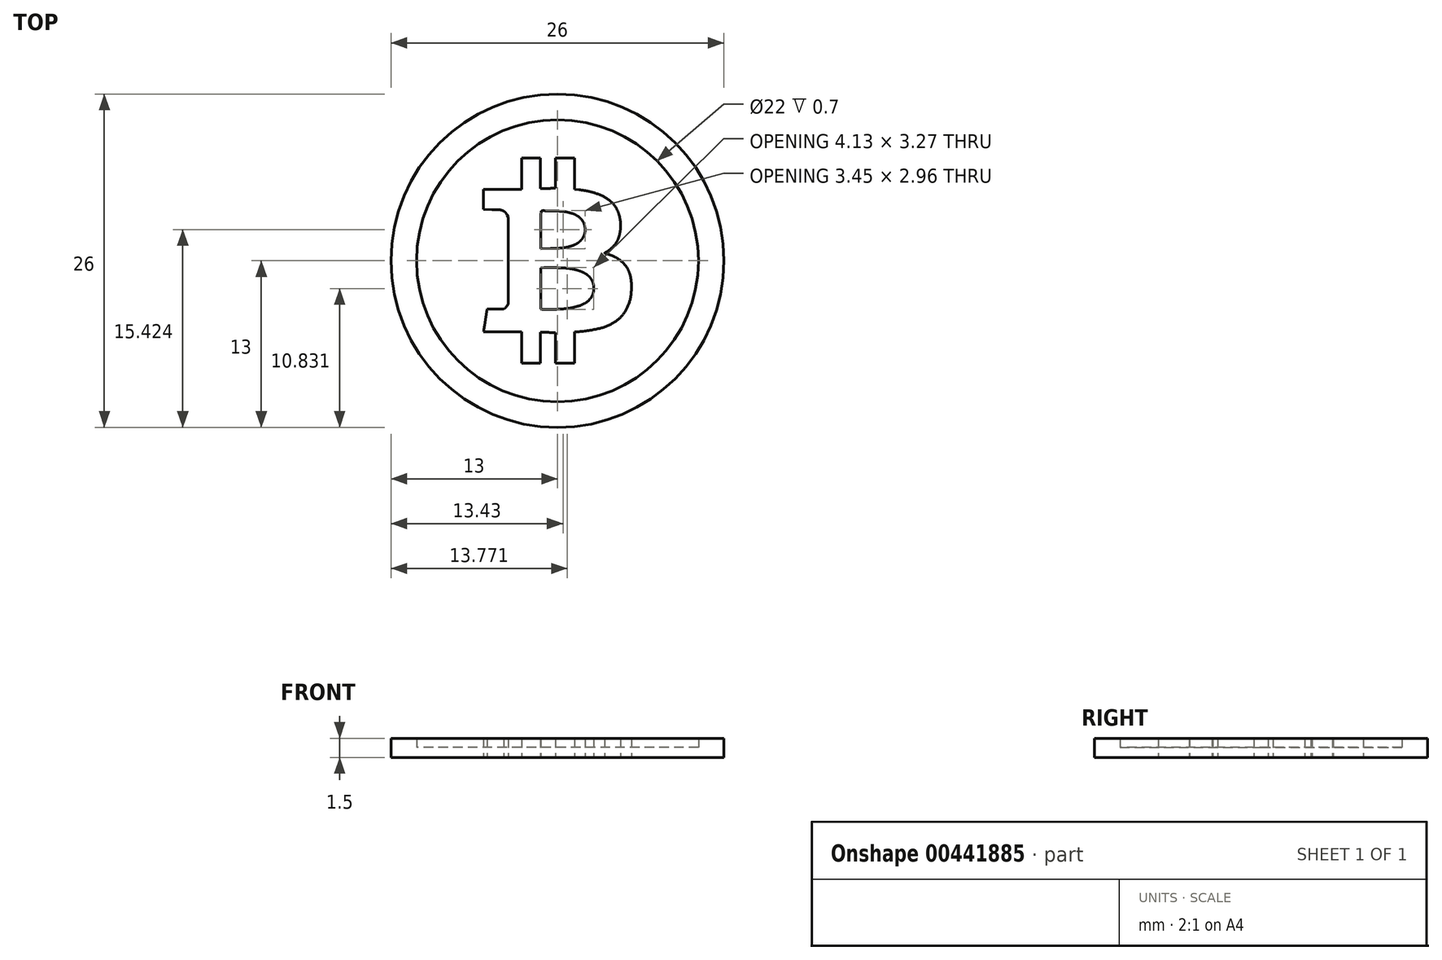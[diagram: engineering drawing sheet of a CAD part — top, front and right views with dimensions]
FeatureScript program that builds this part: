
annotation { "Feature Type Name" : "Feature", "Feature Type Description" : "" }
export const myFeature = defineFeature(function(context is Context, id is Id, definition is map)
    precondition{}
    {
        {
            var Q0;
            Q0=qCreatedBy(makeId("Top.planeOp"),FACE);
            var sketch = newSketch(context, id + "F0", { "sketchPlane" : qUnion([Q0])});
            skCircle(sketch, "E0", {"center": v(0, 0) * mm, "radius": 13 * mm});
            skCircle(sketch, "E1", {"center": v(0, 0) * mm, "radius": 11 * mm});
            skSolve(sketch);
        }
        {
            var Q0;
            Q0=makeQuery(id+"F0.imprint","IMPRINT",FACE,{"disambiguationData":[TD([[makeQuery(id+"F0.imprint","IMPRINT",EDGE,{"derivedFrom":sQuery(id+"F0.wireOp",EDGE,"E1")}),1.0]])]});
            extrude(context, id + "F1", {"entities" : qUnion([Q0]), "depth" : 0.8 * mm});
        }
        {
            var Q0;
            Q0 = qSketchRegion(id + "F0", true);
            extrude(context, id + "F2", {"entities" : qUnion([Q0]), "operationType" : NewBodyOperationType.ADD, "depth" : 1.5 * mm});
        }
        {
            var Q0;
            Q0=qCreatedBy(makeId("Top.planeOp"),FACE);
            var sketch = newSketch(context, id + "F3", { "sketchPlane" : qUnion([Q0])});
            skLineSegment(sketch, "E2", {"start": v(-111.79, 271.5) * mm, "end": v(-111.79, 223) * mm});
            skLineSegment(sketch, "E3", {"start": v(-111.79, 223) * mm, "end": v(-171.29, 223) * mm});
            skLineSegment(sketch, "E4", {"start": v(-171.29, 223) * mm, "end": v(-230.79, 223) * mm});
            skLineSegment(sketch, "E5", {"start": v(-230.79, 223) * mm, "end": v(-230.79, 191.59) * mm});
            skLineSegment(sketch, "E6", {"start": v(-230.79, 191.59) * mm, "end": v(-230.79, 160.17) * mm});
            skLineSegment(sketch, "E7", {"start": v(-230.79, 160.17) * mm, "end": v(-204.54, 159.8) * mm});
            skArc(sketch, "E8", {"start": v(-204.54, 159.8) * mm, "mid": v(-196.82, 159.67) * mm, "end": v(-189.1, 159.51) * mm});
            skArc(sketch, "E9", {"start": v(-189.1, 159.51) * mm, "mid": v(-185.4, 159.38) * mm, "end": v(-181.7, 159.14) * mm});
            skArc(sketch, "E10", {"start": v(-181.7, 159.14) * mm, "mid": v(-179.35, 158.9) * mm, "end": v(-177.03, 158.5) * mm});
            skArc(sketch, "E11", {"start": v(-177.03, 158.5) * mm, "mid": v(-175.06, 158.02) * mm, "end": v(-173.16, 157.35) * mm});
            skArc(sketch, "E12", {"start": v(-173.16, 157.35) * mm, "mid": v(-170.43, 156.14) * mm, "end": v(-167.78, 154.75) * mm});
            skArc(sketch, "E13", {"start": v(-167.78, 154.75) * mm, "mid": v(-165.66, 153.39) * mm, "end": v(-163.7, 151.8) * mm});
            skArc(sketch, "E14", {"start": v(-163.7, 151.8) * mm, "mid": v(-161.97, 150.03) * mm, "end": v(-160.44, 148.07) * mm});
            skArc(sketch, "E15", {"start": v(-160.44, 148.07) * mm, "mid": v(-158.9, 145.67) * mm, "end": v(-157.55, 143.16) * mm});
            skLineSegment(sketch, "E16", {"start": v(-157.55, 143.16) * mm, "end": v(-154.29, 136.54) * mm});
            skLineSegment(sketch, "E17", {"start": v(-154.29, 136.54) * mm, "end": v(-154.29, 1.02) * mm});
            skLineSegment(sketch, "E18", {"start": v(-154.29, 1.02) * mm, "end": v(-154.29, -134.5) * mm});
            skLineSegment(sketch, "E19", {"start": v(-154.29, -134.5) * mm, "end": v(-156.79, -139.5) * mm});
            skArc(sketch, "E20", {"start": v(-156.79, -139.5) * mm, "mid": v(-157.42, -140.67) * mm, "end": v(-158.13, -141.8) * mm});
            skArc(sketch, "E21", {"start": v(-158.13, -141.8) * mm, "mid": v(-158.92, -142.9) * mm, "end": v(-159.77, -143.96) * mm});
            skArc(sketch, "E22", {"start": v(-159.77, -143.96) * mm, "mid": v(-160.67, -144.96) * mm, "end": v(-161.63, -145.9) * mm});
            skArc(sketch, "E23", {"start": v(-161.63, -145.9) * mm, "mid": v(-162.6, -146.73) * mm, "end": v(-163.62, -147.5) * mm});
            skLineSegment(sketch, "E24", {"start": v(-163.62, -147.5) * mm, "end": v(-167.96, -150.5) * mm});
            skLineSegment(sketch, "E25", {"start": v(-167.96, -150.5) * mm, "end": v(-193.68, -150.81) * mm});
            skLineSegment(sketch, "E26", {"start": v(-193.68, -150.81) * mm, "end": v(-219.4, -151.12) * mm});
            skLineSegment(sketch, "E27", {"start": v(-219.4, -151.12) * mm, "end": v(-224.7, -183.81) * mm});
            skArc(sketch, "E28", {"start": v(-224.7, -183.81) * mm, "mid": v(-225.73, -190.17) * mm, "end": v(-226.76, -196.54) * mm});
            skArc(sketch, "E29", {"start": v(-226.76, -196.54) * mm, "mid": v(-227.67, -202.12) * mm, "end": v(-228.59, -207.7) * mm});
            skArc(sketch, "E30", {"start": v(-228.59, -207.7) * mm, "mid": v(-229.37, -212.47) * mm, "end": v(-230.15, -217.24) * mm});
            skArc(sketch, "E31", {"start": v(-230.15, -217.24) * mm, "mid": v(-230.33, -218.24) * mm, "end": v(-230.51, -219.25) * mm});
            skLineSegment(sketch, "E32", {"start": v(-230.51, -219.25) * mm, "end": v(-231.04, -222) * mm});
            skLineSegment(sketch, "E33", {"start": v(-231.04, -222) * mm, "end": v(-171.41, -222) * mm});
            skLineSegment(sketch, "E34", {"start": v(-171.41, -222) * mm, "end": v(-111.79, -222) * mm});
            skLineSegment(sketch, "E35", {"start": v(-111.79, -222) * mm, "end": v(-111.79, -271) * mm});
            skLineSegment(sketch, "E36", {"start": v(-111.79, -271) * mm, "end": v(-111.79, -320) * mm});
            skLineSegment(sketch, "E37", {"start": v(-111.79, -320) * mm, "end": v(-82.29, -320) * mm});
            skLineSegment(sketch, "E38", {"start": v(-82.29, -320) * mm, "end": v(-52.79, -320) * mm});
            skLineSegment(sketch, "E39", {"start": v(-52.79, -320) * mm, "end": v(-52.79, -271.34) * mm});
            skLineSegment(sketch, "E40", {"start": v(-52.79, -271.34) * mm, "end": v(-52.79, -222.69) * mm});
            skLineSegment(sketch, "E41", {"start": v(-52.79, -222.69) * mm, "end": v(-35.54, -223.34) * mm});
            skArc(sketch, "E42", {"start": v(-35.54, -223.34) * mm, "mid": v(-32, -223.47) * mm, "end": v(-28.48, -223.6) * mm});
            skArc(sketch, "E43", {"start": v(-28.48, -223.6) * mm, "mid": v(-25, -223.7) * mm, "end": v(-21.52, -223.8) * mm});
            skArc(sketch, "E44", {"start": v(-21.52, -223.8) * mm, "mid": v(-18.52, -223.88) * mm, "end": v(-15.51, -223.96) * mm});
            skArc(sketch, "E45", {"start": v(-15.51, -223.96) * mm, "mid": v(-13.78, -223.99) * mm, "end": v(-12.04, -224) * mm});
            skLineSegment(sketch, "E46", {"start": v(-12.04, -224) * mm, "end": v(-5.79, -224) * mm});
            skLineSegment(sketch, "E47", {"start": v(-5.79, -224) * mm, "end": v(-5.79, -272) * mm});
            skLineSegment(sketch, "E48", {"start": v(-5.79, -272) * mm, "end": v(-5.79, -320) * mm});
            skLineSegment(sketch, "E49", {"start": v(-5.79, -320) * mm, "end": v(23.71, -320) * mm});
            skLineSegment(sketch, "E50", {"start": v(23.71, -320) * mm, "end": v(53.21, -320) * mm});
            skLineSegment(sketch, "E51", {"start": v(53.21, -320) * mm, "end": v(53.21, -271.14) * mm});
            skLineSegment(sketch, "E52", {"start": v(53.21, -271.14) * mm, "end": v(53.21, -222.27) * mm});
            skLineSegment(sketch, "E53", {"start": v(53.21, -222.27) * mm, "end": v(62.96, -221.59) * mm});
            skArc(sketch, "E54", {"start": v(62.96, -221.59) * mm, "mid": v(97.45, -217.74) * mm, "end": v(131.53, -211.13) * mm});
            skArc(sketch, "E55", {"start": v(131.53, -211.13) * mm, "mid": v(156.79, -202.75) * mm, "end": v(180.2, -190.07) * mm});
            skArc(sketch, "E56", {"start": v(180.2, -190.07) * mm, "mid": v(197.76, -175.43) * mm, "end": v(211.68, -157.3) * mm});
            skArc(sketch, "E57", {"start": v(211.68, -157.3) * mm, "mid": v(222.29, -135.43) * mm, "end": v(228.69, -112) * mm});
            skArc(sketch, "E58", {"start": v(228.69, -112) * mm, "mid": v(229.06, -109.66) * mm, "end": v(229.37, -107.3) * mm});
            skArc(sketch, "E59", {"start": v(229.37, -107.3) * mm, "mid": v(229.72, -104.08) * mm, "end": v(230.03, -100.85) * mm});
            skArc(sketch, "E60", {"start": v(230.03, -100.85) * mm, "mid": v(230.33, -97.36) * mm, "end": v(230.58, -93.86) * mm});
            skArc(sketch, "E61", {"start": v(230.58, -93.86) * mm, "mid": v(230.78, -90.62) * mm, "end": v(230.92, -87.38) * mm});
            skArc(sketch, "E62", {"start": v(230.92, -87.38) * mm, "mid": v(230.7, -70.42) * mm, "end": v(228.76, -53.56) * mm});
            skArc(sketch, "E63", {"start": v(228.76, -53.56) * mm, "mid": v(225.24, -39.46) * mm, "end": v(219.52, -26.1) * mm});
            skArc(sketch, "E64", {"start": v(219.52, -26.1) * mm, "mid": v(212.07, -14.5) * mm, "end": v(202.75, -4.37) * mm});
            skArc(sketch, "E65", {"start": v(202.75, -4.37) * mm, "mid": v(191.14, 4.87) * mm, "end": v(178.37, 12.43) * mm});
            skArc(sketch, "E66", {"start": v(178.37, 12.43) * mm, "mid": v(175, 14.03) * mm, "end": v(171.57, 15.48) * mm});
            skArc(sketch, "E67", {"start": v(171.57, 15.48) * mm, "mid": v(166.77, 17.34) * mm, "end": v(161.94, 19.11) * mm});
            skArc(sketch, "E68", {"start": v(161.94, 19.11) * mm, "mid": v(157.15, 20.8) * mm, "end": v(152.34, 22.43) * mm});
            skArc(sketch, "E69", {"start": v(152.34, 22.43) * mm, "mid": v(150.6, 22.86) * mm, "end": v(148.83, 23) * mm});
            skArc(sketch, "E70", {"start": v(148.83, 23) * mm, "mid": v(148.25, 23.1) * mm, "end": v(147.73, 23.4) * mm});
            skArc(sketch, "E71", {"start": v(147.73, 23.4) * mm, "mid": v(147.53, 23.77) * mm, "end": v(147.67, 24.16) * mm});
            skArc(sketch, "E72", {"start": v(147.67, 24.16) * mm, "mid": v(148.47, 24.94) * mm, "end": v(149.37, 25.6) * mm});
            skArc(sketch, "E73", {"start": v(149.37, 25.6) * mm, "mid": v(151.31, 26.79) * mm, "end": v(153.27, 27.94) * mm});
            skArc(sketch, "E74", {"start": v(153.27, 27.94) * mm, "mid": v(157.98, 30.87) * mm, "end": v(162.46, 34.13) * mm});
            skArc(sketch, "E75", {"start": v(162.46, 34.13) * mm, "mid": v(167.05, 37.98) * mm, "end": v(171.42, 42.08) * mm});
            skArc(sketch, "E76", {"start": v(171.42, 42.08) * mm, "mid": v(175.53, 46.42) * mm, "end": v(179.39, 51) * mm});
            skArc(sketch, "E77", {"start": v(179.39, 51) * mm, "mid": v(182.66, 55.45) * mm, "end": v(185.6, 60.14) * mm});
            skArc(sketch, "E78", {"start": v(185.6, 60.14) * mm, "mid": v(188.11, 65) * mm, "end": v(190.18, 70.07) * mm});
            skArc(sketch, "E79", {"start": v(190.18, 70.07) * mm, "mid": v(192.2, 76.3) * mm, "end": v(193.9, 82.64) * mm});
            skArc(sketch, "E80", {"start": v(193.9, 82.64) * mm, "mid": v(195.32, 89.32) * mm, "end": v(196.39, 96.06) * mm});
            skArc(sketch, "E81", {"start": v(196.39, 96.06) * mm, "mid": v(197, 102.33) * mm, "end": v(197.2, 108.63) * mm});
            skArc(sketch, "E82", {"start": v(197.2, 108.63) * mm, "mid": v(195.94, 126.5) * mm, "end": v(192.21, 144.03) * mm});
            skArc(sketch, "E83", {"start": v(192.21, 144.03) * mm, "mid": v(186.31, 159.12) * mm, "end": v(177.7, 172.86) * mm});
            skArc(sketch, "E84", {"start": v(177.7, 172.86) * mm, "mid": v(166.49, 185.05) * mm, "end": v(153.26, 195.03) * mm});
            skArc(sketch, "E85", {"start": v(153.26, 195.03) * mm, "mid": v(136.62, 203.98) * mm, "end": v(119.02, 210.82) * mm});
            skArc(sketch, "E86", {"start": v(119.02, 210.82) * mm, "mid": v(113.11, 212.62) * mm, "end": v(107.16, 214.26) * mm});
            skArc(sketch, "E87", {"start": v(107.16, 214.26) * mm, "mid": v(100.9, 215.8) * mm, "end": v(94.63, 217.2) * mm});
            skArc(sketch, "E88", {"start": v(94.63, 217.2) * mm, "mid": v(88.03, 218.5) * mm, "end": v(81.4, 219.66) * mm});
            skArc(sketch, "E89", {"start": v(81.4, 219.66) * mm, "mid": v(74.44, 220.72) * mm, "end": v(67.46, 221.63) * mm});
            skLineSegment(sketch, "E90", {"start": v(67.46, 221.63) * mm, "end": v(53.21, 223.35) * mm});
            skLineSegment(sketch, "E91", {"start": v(53.21, 223.35) * mm, "end": v(53.21, 271.68) * mm});
            skLineSegment(sketch, "E92", {"start": v(53.21, 271.68) * mm, "end": v(53.21, 320) * mm});
            skLineSegment(sketch, "E93", {"start": v(53.21, 320) * mm, "end": v(23.71, 320) * mm});
            skLineSegment(sketch, "E94", {"start": v(23.71, 320) * mm, "end": v(-5.79, 320) * mm});
            skLineSegment(sketch, "E95", {"start": v(-5.79, 320) * mm, "end": v(-5.79, 273) * mm});
            skLineSegment(sketch, "E96", {"start": v(-5.79, 273) * mm, "end": v(-5.79, 226) * mm});
            skLineSegment(sketch, "E97", {"start": v(-5.79, 226) * mm, "end": v(-15.04, 226) * mm});
            skArc(sketch, "E98", {"start": v(-15.04, 226) * mm, "mid": v(-17.3, 225.98) * mm, "end": v(-19.58, 225.95) * mm});
            skArc(sketch, "E99", {"start": v(-19.58, 225.95) * mm, "mid": v(-22.67, 225.88) * mm, "end": v(-25.76, 225.8) * mm});
            skArc(sketch, "E100", {"start": v(-25.76, 225.8) * mm, "mid": v(-29.08, 225.7) * mm, "end": v(-32.4, 225.6) * mm});
            skArc(sketch, "E101", {"start": v(-32.4, 225.6) * mm, "mid": v(-35.47, 225.47) * mm, "end": v(-38.54, 225.34) * mm});
            skLineSegment(sketch, "E102", {"start": v(-38.54, 225.34) * mm, "end": v(-52.79, 224.69) * mm});
            skLineSegment(sketch, "E103", {"start": v(-52.79, 224.69) * mm, "end": v(-52.79, 272.34) * mm});
            skLineSegment(sketch, "E104", {"start": v(-52.79, 272.34) * mm, "end": v(-52.79, 320) * mm});
            skLineSegment(sketch, "E105", {"start": v(-52.79, 320) * mm, "end": v(-82.29, 320) * mm});
            skLineSegment(sketch, "E106", {"start": v(-82.29, 320) * mm, "end": v(-111.79, 320) * mm});
            skLineSegment(sketch, "E107", {"start": v(-111.79, 320) * mm, "end": v(-111.79, 271.5) * mm});
            skArc(sketch, "E108", {"start": v(21.03, 153.53) * mm, "mid": v(33.98, 150.93) * mm, "end": v(46.66, 147.27) * mm});
            skArc(sketch, "E109", {"start": v(46.66, 147.27) * mm, "mid": v(56.59, 143.11) * mm, "end": v(65.78, 137.51) * mm});
            skArc(sketch, "E110", {"start": v(65.78, 137.51) * mm, "mid": v(72.75, 131.46) * mm, "end": v(78.48, 124.24) * mm});
            skArc(sketch, "E111", {"start": v(78.48, 124.24) * mm, "mid": v(82.64, 116.23) * mm, "end": v(85.13, 107.57) * mm});
            skArc(sketch, "E112", {"start": v(85.13, 107.57) * mm, "mid": v(85.98, 101.07) * mm, "end": v(86.19, 94.52) * mm});
            skArc(sketch, "E113", {"start": v(86.19, 94.52) * mm, "mid": v(85.68, 88.64) * mm, "end": v(84.39, 82.87) * mm});
            skArc(sketch, "E114", {"start": v(84.39, 82.87) * mm, "mid": v(82.35, 77.4) * mm, "end": v(79.58, 72.28) * mm});
            skArc(sketch, "E115", {"start": v(79.58, 72.28) * mm, "mid": v(75.93, 67.12) * mm, "end": v(71.73, 62.4) * mm});
            skArc(sketch, "E116", {"start": v(71.73, 62.4) * mm, "mid": v(68.5, 59.37) * mm, "end": v(65.05, 56.6) * mm});
            skArc(sketch, "E117", {"start": v(65.05, 56.6) * mm, "mid": v(61.34, 54.07) * mm, "end": v(57.46, 51.81) * mm});
            skArc(sketch, "E118", {"start": v(57.46, 51.81) * mm, "mid": v(53.11, 49.68) * mm, "end": v(48.63, 47.85) * mm});
            skArc(sketch, "E119", {"start": v(48.63, 47.85) * mm, "mid": v(43.45, 46.08) * mm, "end": v(38.2, 44.55) * mm});
            skArc(sketch, "E120", {"start": v(38.2, 44.55) * mm, "mid": v(31.88, 42.98) * mm, "end": v(25.52, 41.63) * mm});
            skArc(sketch, "E121", {"start": v(25.52, 41.63) * mm, "mid": v(19.68, 40.62) * mm, "end": v(13.8, 39.87) * mm});
            skArc(sketch, "E122", {"start": v(13.8, 39.87) * mm, "mid": v(6.76, 39.25) * mm, "end": v(-0.3, 38.86) * mm});
            skArc(sketch, "E123", {"start": v(-0.3, 38.86) * mm, "mid": v(-10.92, 38.52) * mm, "end": v(-21.54, 38.28) * mm});
            skLineSegment(sketch, "E124", {"start": v(-21.54, 38.28) * mm, "end": v(-51.79, 37.75) * mm});
            skLineSegment(sketch, "E125", {"start": v(-51.79, 37.75) * mm, "end": v(-51.79, 96.3) * mm});
            skArc(sketch, "E126", {"start": v(-51.79, 96.3) * mm, "mid": v(-51.78, 114.38) * mm, "end": v(-51.75, 132.46) * mm});
            skArc(sketch, "E127", {"start": v(-51.75, 132.46) * mm, "mid": v(-51.69, 139.35) * mm, "end": v(-51.53, 146.24) * mm});
            skArc(sketch, "E128", {"start": v(-51.53, 146.24) * mm, "mid": v(-51.38, 150.11) * mm, "end": v(-51.15, 153.98) * mm});
            skArc(sketch, "E129", {"start": v(-51.15, 153.98) * mm, "mid": v(-50.81, 154.85) * mm, "end": v(-50.04, 155.38) * mm});
            skArc(sketch, "E130", {"start": v(-50.04, 155.38) * mm, "mid": v(-47.25, 155.98) * mm, "end": v(-44.4, 156.15) * mm});
            skArc(sketch, "E131", {"start": v(-44.4, 156.15) * mm, "mid": v(-30.57, 155.86) * mm, "end": v(-16.75, 155.52) * mm});
            skArc(sketch, "E132", {"start": v(-16.75, 155.52) * mm, "mid": v(-3.61, 155.14) * mm, "end": v(9.52, 154.67) * mm});
            skArc(sketch, "E133", {"start": v(9.52, 154.67) * mm, "mid": v(15.3, 154.27) * mm, "end": v(21.03, 153.53) * mm});
            skArc(sketch, "E134", {"start": v(30.21, -23.44) * mm, "mid": v(42.62, -25.24) * mm, "end": v(54.91, -27.67) * mm});
            skArc(sketch, "E135", {"start": v(54.91, -27.67) * mm, "mid": v(65.12, -30.43) * mm, "end": v(75.05, -34.04) * mm});
            skArc(sketch, "E136", {"start": v(75.05, -34.04) * mm, "mid": v(83.16, -37.9) * mm, "end": v(90.82, -42.55) * mm});
            skArc(sketch, "E137", {"start": v(90.82, -42.55) * mm, "mid": v(96.96, -47.44) * mm, "end": v(102.29, -53.22) * mm});
            skArc(sketch, "E138", {"start": v(102.29, -53.22) * mm, "mid": v(104.9, -56.81) * mm, "end": v(107.24, -60.6) * mm});
            skArc(sketch, "E139", {"start": v(107.24, -60.6) * mm, "mid": v(109.13, -64.38) * mm, "end": v(110.68, -68.31) * mm});
            skArc(sketch, "E140", {"start": v(110.68, -68.31) * mm, "mid": v(111.88, -72.44) * mm, "end": v(112.7, -76.67) * mm});
            skArc(sketch, "E141", {"start": v(112.7, -76.67) * mm, "mid": v(113.24, -81.32) * mm, "end": v(113.45, -86) * mm});
            skArc(sketch, "E142", {"start": v(113.45, -86) * mm, "mid": v(112.15, -98) * mm, "end": v(108.1, -109.37) * mm});
            skArc(sketch, "E143", {"start": v(108.1, -109.37) * mm, "mid": v(101.52, -119.5) * mm, "end": v(92.78, -127.83) * mm});
            skArc(sketch, "E144", {"start": v(92.78, -127.83) * mm, "mid": v(80.33, -135.58) * mm, "end": v(66.72, -141.05) * mm});
            skArc(sketch, "E145", {"start": v(66.72, -141.05) * mm, "mid": v(48.38, -145.77) * mm, "end": v(29.71, -148.96) * mm});
            skArc(sketch, "E146", {"start": v(29.71, -148.96) * mm, "mid": v(21.14, -149.9) * mm, "end": v(12.54, -150.55) * mm});
            skArc(sketch, "E147", {"start": v(12.54, -150.55) * mm, "mid": v(0.42, -151.17) * mm, "end": v(-11.71, -151.63) * mm});
            skArc(sketch, "E148", {"start": v(-11.71, -151.63) * mm, "mid": v(-23.56, -151.93) * mm, "end": v(-35.4, -152.1) * mm});
            skArc(sketch, "E149", {"start": v(-35.4, -152.1) * mm, "mid": v(-41.29, -151.95) * mm, "end": v(-47.15, -151.36) * mm});
            skLineSegment(sketch, "E150", {"start": v(-47.15, -151.36) * mm, "end": v(-51.79, -150.73) * mm});
            skLineSegment(sketch, "E151", {"start": v(-51.79, -150.73) * mm, "end": v(-51.79, -86.4) * mm});
            skLineSegment(sketch, "E152", {"start": v(-51.79, -86.4) * mm, "end": v(-51.79, -22.07) * mm});
            skLineSegment(sketch, "E153", {"start": v(-51.79, -22.07) * mm, "end": v(-41.54, -21.67) * mm});
            skArc(sketch, "E154", {"start": v(-41.54, -21.67) * mm, "mid": v(-33.33, -21.44) * mm, "end": v(-25.12, -21.4) * mm});
            skArc(sketch, "E155", {"start": v(-25.12, -21.4) * mm, "mid": v(-14.26, -21.5) * mm, "end": v(-3.4, -21.72) * mm});
            skArc(sketch, "E156", {"start": v(-3.4, -21.72) * mm, "mid": v(7.1, -22.02) * mm, "end": v(17.6, -22.42) * mm});
            skArc(sketch, "E157", {"start": v(17.6, -22.42) * mm, "mid": v(23.92, -22.81) * mm, "end": v(30.21, -23.44) * mm});
            skSolve(sketch);
        }
        {
            var Q0;
            Q0 = qSketchRegion(id + "F3", true);
            extrude(context, id + "F4", {"entities" : qUnion([Q0]), "depth" : 60 * mm});
        }
        {
            var Q0;
            Q0=makeQuery(id+"F4.opExtrude","SWEPT_BODY",BODY,{"disambiguationData":[OSD([sQuery(id+"F3.wireOp",EDGE,"E2"),sQuery(id+"F3.wireOp",EDGE,"E3"),sQuery(id+"F3.wireOp",EDGE,"E4"),sQuery(id+"F3.wireOp",EDGE,"E5"),sQuery(id+"F3.wireOp",EDGE,"E6"),sQuery(id+"F3.wireOp",EDGE,"E7"),sQuery(id+"F3.wireOp",EDGE,"E8"),sQuery(id+"F3.wireOp",EDGE,"E9"),sQuery(id+"F3.wireOp",EDGE,"E10"),sQuery(id+"F3.wireOp",EDGE,"E11"),sQuery(id+"F3.wireOp",EDGE,"E12"),sQuery(id+"F3.wireOp",EDGE,"E13"),sQuery(id+"F3.wireOp",EDGE,"E14"),sQuery(id+"F3.wireOp",EDGE,"E15"),sQuery(id+"F3.wireOp",EDGE,"E16"),sQuery(id+"F3.wireOp",EDGE,"E17"),sQuery(id+"F3.wireOp",EDGE,"E18"),sQuery(id+"F3.wireOp",EDGE,"E19"),sQuery(id+"F3.wireOp",EDGE,"E20"),sQuery(id+"F3.wireOp",EDGE,"E21"),sQuery(id+"F3.wireOp",EDGE,"E22"),sQuery(id+"F3.wireOp",EDGE,"E23"),sQuery(id+"F3.wireOp",EDGE,"E24"),sQuery(id+"F3.wireOp",EDGE,"E25"),sQuery(id+"F3.wireOp",EDGE,"E26"),sQuery(id+"F3.wireOp",EDGE,"E27"),sQuery(id+"F3.wireOp",EDGE,"E28"),sQuery(id+"F3.wireOp",EDGE,"E29"),sQuery(id+"F3.wireOp",EDGE,"E30"),sQuery(id+"F3.wireOp",EDGE,"E31"),sQuery(id+"F3.wireOp",EDGE,"E32"),sQuery(id+"F3.wireOp",EDGE,"E33"),sQuery(id+"F3.wireOp",EDGE,"E34"),sQuery(id+"F3.wireOp",EDGE,"E35"),sQuery(id+"F3.wireOp",EDGE,"E36"),sQuery(id+"F3.wireOp",EDGE,"E37"),sQuery(id+"F3.wireOp",EDGE,"E38"),sQuery(id+"F3.wireOp",EDGE,"E39"),sQuery(id+"F3.wireOp",EDGE,"E40"),sQuery(id+"F3.wireOp",EDGE,"E41"),sQuery(id+"F3.wireOp",EDGE,"E42"),sQuery(id+"F3.wireOp",EDGE,"E43"),sQuery(id+"F3.wireOp",EDGE,"E44"),sQuery(id+"F3.wireOp",EDGE,"E45"),sQuery(id+"F3.wireOp",EDGE,"E46"),sQuery(id+"F3.wireOp",EDGE,"E47"),sQuery(id+"F3.wireOp",EDGE,"E48"),sQuery(id+"F3.wireOp",EDGE,"E49"),sQuery(id+"F3.wireOp",EDGE,"E50"),sQuery(id+"F3.wireOp",EDGE,"E51"),sQuery(id+"F3.wireOp",EDGE,"E52"),sQuery(id+"F3.wireOp",EDGE,"E53"),sQuery(id+"F3.wireOp",EDGE,"E54"),sQuery(id+"F3.wireOp",EDGE,"E55"),sQuery(id+"F3.wireOp",EDGE,"E56"),sQuery(id+"F3.wireOp",EDGE,"E57"),sQuery(id+"F3.wireOp",EDGE,"E58"),sQuery(id+"F3.wireOp",EDGE,"E59"),sQuery(id+"F3.wireOp",EDGE,"E60"),sQuery(id+"F3.wireOp",EDGE,"E61"),sQuery(id+"F3.wireOp",EDGE,"E62"),sQuery(id+"F3.wireOp",EDGE,"E63"),sQuery(id+"F3.wireOp",EDGE,"E64"),sQuery(id+"F3.wireOp",EDGE,"E65"),sQuery(id+"F3.wireOp",EDGE,"E66"),sQuery(id+"F3.wireOp",EDGE,"E67"),sQuery(id+"F3.wireOp",EDGE,"E68"),sQuery(id+"F3.wireOp",EDGE,"E69"),sQuery(id+"F3.wireOp",EDGE,"E70"),sQuery(id+"F3.wireOp",EDGE,"E71"),sQuery(id+"F3.wireOp",EDGE,"E72"),sQuery(id+"F3.wireOp",EDGE,"E73"),sQuery(id+"F3.wireOp",EDGE,"E74"),sQuery(id+"F3.wireOp",EDGE,"E75"),sQuery(id+"F3.wireOp",EDGE,"E76"),sQuery(id+"F3.wireOp",EDGE,"E77"),sQuery(id+"F3.wireOp",EDGE,"E78"),sQuery(id+"F3.wireOp",EDGE,"E79"),sQuery(id+"F3.wireOp",EDGE,"E80"),sQuery(id+"F3.wireOp",EDGE,"E81"),sQuery(id+"F3.wireOp",EDGE,"E82"),sQuery(id+"F3.wireOp",EDGE,"E83"),sQuery(id+"F3.wireOp",EDGE,"E84"),sQuery(id+"F3.wireOp",EDGE,"E85"),sQuery(id+"F3.wireOp",EDGE,"E86"),sQuery(id+"F3.wireOp",EDGE,"E87"),sQuery(id+"F3.wireOp",EDGE,"E88"),sQuery(id+"F3.wireOp",EDGE,"E89"),sQuery(id+"F3.wireOp",EDGE,"E90"),sQuery(id+"F3.wireOp",EDGE,"E91"),sQuery(id+"F3.wireOp",EDGE,"E92"),sQuery(id+"F3.wireOp",EDGE,"E93"),sQuery(id+"F3.wireOp",EDGE,"E94"),sQuery(id+"F3.wireOp",EDGE,"E95"),sQuery(id+"F3.wireOp",EDGE,"E96"),sQuery(id+"F3.wireOp",EDGE,"E97"),sQuery(id+"F3.wireOp",EDGE,"E98"),sQuery(id+"F3.wireOp",EDGE,"E99"),sQuery(id+"F3.wireOp",EDGE,"E100"),sQuery(id+"F3.wireOp",EDGE,"E101"),sQuery(id+"F3.wireOp",EDGE,"E102"),sQuery(id+"F3.wireOp",EDGE,"E103"),sQuery(id+"F3.wireOp",EDGE,"E104"),sQuery(id+"F3.wireOp",EDGE,"E105"),sQuery(id+"F3.wireOp",EDGE,"E106"),sQuery(id+"F3.wireOp",EDGE,"E107"),sQuery(id+"F3.wireOp",EDGE,"E108"),sQuery(id+"F3.wireOp",EDGE,"E109"),sQuery(id+"F3.wireOp",EDGE,"E110"),sQuery(id+"F3.wireOp",EDGE,"E111"),sQuery(id+"F3.wireOp",EDGE,"E112"),sQuery(id+"F3.wireOp",EDGE,"E113"),sQuery(id+"F3.wireOp",EDGE,"E114"),sQuery(id+"F3.wireOp",EDGE,"E115"),sQuery(id+"F3.wireOp",EDGE,"E116"),sQuery(id+"F3.wireOp",EDGE,"E117"),sQuery(id+"F3.wireOp",EDGE,"E118"),sQuery(id+"F3.wireOp",EDGE,"E119"),sQuery(id+"F3.wireOp",EDGE,"E120"),sQuery(id+"F3.wireOp",EDGE,"E121"),sQuery(id+"F3.wireOp",EDGE,"E122"),sQuery(id+"F3.wireOp",EDGE,"E123"),sQuery(id+"F3.wireOp",EDGE,"E124"),sQuery(id+"F3.wireOp",EDGE,"E125"),sQuery(id+"F3.wireOp",EDGE,"E126"),sQuery(id+"F3.wireOp",EDGE,"E127"),sQuery(id+"F3.wireOp",EDGE,"E128"),sQuery(id+"F3.wireOp",EDGE,"E129"),sQuery(id+"F3.wireOp",EDGE,"E130"),sQuery(id+"F3.wireOp",EDGE,"E131"),sQuery(id+"F3.wireOp",EDGE,"E132"),sQuery(id+"F3.wireOp",EDGE,"E133"),sQuery(id+"F3.wireOp",EDGE,"E134"),sQuery(id+"F3.wireOp",EDGE,"E135"),sQuery(id+"F3.wireOp",EDGE,"E136"),sQuery(id+"F3.wireOp",EDGE,"E137"),sQuery(id+"F3.wireOp",EDGE,"E138"),sQuery(id+"F3.wireOp",EDGE,"E139"),sQuery(id+"F3.wireOp",EDGE,"E140"),sQuery(id+"F3.wireOp",EDGE,"E141"),sQuery(id+"F3.wireOp",EDGE,"E142"),sQuery(id+"F3.wireOp",EDGE,"E143"),sQuery(id+"F3.wireOp",EDGE,"E144"),sQuery(id+"F3.wireOp",EDGE,"E145"),sQuery(id+"F3.wireOp",EDGE,"E146"),sQuery(id+"F3.wireOp",EDGE,"E147"),sQuery(id+"F3.wireOp",EDGE,"E148"),sQuery(id+"F3.wireOp",EDGE,"E149"),sQuery(id+"F3.wireOp",EDGE,"E150"),sQuery(id+"F3.wireOp",EDGE,"E151"),sQuery(id+"F3.wireOp",EDGE,"E152"),sQuery(id+"F3.wireOp",EDGE,"E153"),sQuery(id+"F3.wireOp",EDGE,"E154"),sQuery(id+"F3.wireOp",EDGE,"E155"),sQuery(id+"F3.wireOp",EDGE,"E156"),sQuery(id+"F3.wireOp",EDGE,"E157")])]});
            var Q1;
            Q1=qCreatedBy(makeId("Origin.pointOp"),VERTEX);
            transform(context, id + "F5", {"entities" : qUnion([Q0]), "transformType" : TransformType.SCALE_UNIFORMLY, "scale" : 0.03, "scalePoint" : qUnion([Q1]), "makeCopy" : false});
        }
    });
